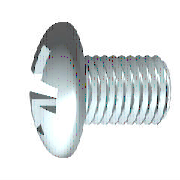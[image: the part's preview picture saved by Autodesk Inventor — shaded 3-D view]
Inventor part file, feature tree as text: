
AUTODESK INVENTOR PART (.ipt)
format: ipt  version: 2011 (Build 150239000, 239)  size: 240,640 bytes
history: native  units: mm (DEFAULTED — no unit token found)
features: extrude x1, other x1, plane x1
ambient origin geometry x7: Origin, YZ Plane, XZ Plane, X Axis, Y Axis, Z Axis, Center Point
bodies: Solid1 (feature_tree), Body (feature_tree)
feature tree (3):
  extrude  "Slot"  Depth=4.1656mm
  other  "Cut"
  plane  "Work Plane3"
